# Revit family: UNB_Mirror+Light_T2907_BIM_FR
name_source: partatom
category: Plumbing Fixtures
revit_build: Autodesk Revit 2017 (Build: 20160225_1515(x64)
units: mm (PartAtom-declared; Revit-internal decimal feet)

## family parameters
Always vertical = Yes
Cut with Voids When Loaded = No
OmniClass Number = 23.45.05.14.21.11
OmniClass Title = Bath/Shower Units
Part Type = Normal
Room Calculation Point = No
Round Connector Dimension = Use Diameter
Shared = No
Work Plane-Based = No

## types (1)
- T2907AA - LIGHT LXY LF1245 344 9W 230V 4000K
    Accessoires = www.idealspec.fr
    Auteur = Ideal Standard
    BOSUseNativeGeometries = 1
    Bim-NomDuProjet = ISI_IdealStandard_BathroomMirrors_UNB_Mirror+Light_T2907
    Caractéristiques = STRADA Lumière 34,4 cm
    CodeBarre = 8014140446729
    Conformité = NF
    ConseilsDInstallation = 0
    Cost = 0 $
    Couleur = Miroir
    CoûtDeRemplacement = 0
    DateDeCréation = 2018_08_03
    Description = STRADA Lumière 34,4 cm
    Dimensions = 43 x 344 x 92mm
    EAN code = https://8014140446729
    Espace = Interne
    Finition = Miroir
    Forme = rectangulaire
    Hauteur = 43 mm
    IfcExportAs = Bathroom mirrors
    IfcExportType = IfcFurnitureType
    InformationsProduit = www.idealspec.fr
    Largeur = 344 mm  [stored 1.12861 ft]
    Longueur = 92 mm  [stored 0.301837 ft]
    Marque = Ideal Standard
    Matériel = 0
    Model = T2907AA
    Nom = BathroomMirrors_UNB_Mirror+Light_T2907_IdealStandard
    PoidsNet = 0,33 KG
    Profondeur = 0 mm  [stored 0 ft]
    Raccordement = Plomberie
    Révision = 1
    URL = www.idealspec.fr
    Uniclass2015Code = Pr_25_71_53_06
    Uniclass2015Title = Bathroom mirrors
    Uniclass2015Version = Products v1.1
    UnitéDeMesure = Millimètres
    UnitéDeTemps = An
    UnitéMonétaire = €
    UrlDuFabricant = www.idealspec.fr
    Version = 1

note: [stored X ft] marks values corroborated as IEEE doubles in the binary element streams (Revit-internal decimal feet)

## geometry (parser evidence)
native form markers: Sweep x3
no freeform markers — native parametric forms only
